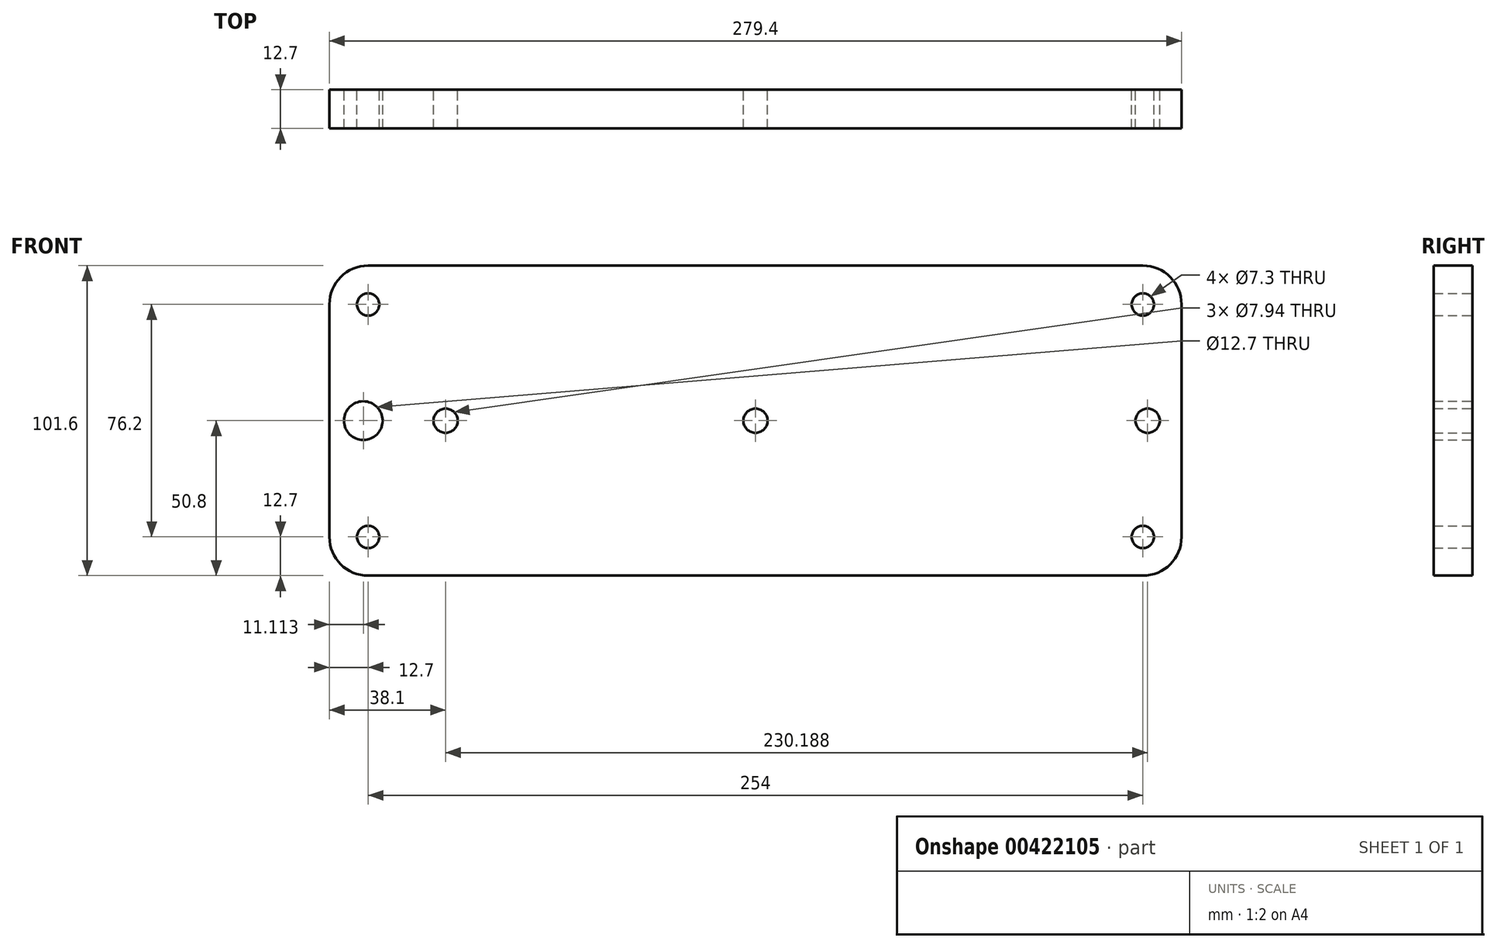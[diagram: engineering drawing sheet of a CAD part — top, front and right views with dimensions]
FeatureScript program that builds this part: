
annotation { "Feature Type Name" : "Feature", "Feature Type Description" : "" }
export const myFeature = defineFeature(function(context is Context, id is Id, definition is map)
    precondition{}
    {
        {
            var Q0;
            Q0=qCreatedBy(makeId("Front.planeOp"),FACE);
            var sketch = newSketch(context, id + "F0", { "sketchPlane" : qUnion([Q0])});
            skLineSegment(sketch, "E0.bottom", {"start": v(12.7, 0) * mm, "end": v(266.7, 0) * mm});
            skLineSegment(sketch, "E0.top", {"start": v(12.7, 101.6) * mm, "end": v(266.7, 101.6) * mm});
            skLineSegment(sketch, "E0.left", {"start": v(0, 12.7) * mm, "end": v(0, 88.9) * mm});
            skLineSegment(sketch, "E0.right", {"start": v(279.4, 12.7) * mm, "end": v(279.4, 88.9) * mm});
            skPoint(sketch, "E1.visualSharp", {"position": v(0, 101.6) * mm});
            skArc(sketch, "E1.filletArc", {"start": v(12.7, 101.6) * mm, "mid": v(3.72, 97.88) * mm, "end": v(0, 88.9) * mm});
            skPoint(sketch, "E2.visualSharp", {"position": v(0, 0) * mm});
            skArc(sketch, "E2.filletArc", {"start": v(0, 12.7) * mm, "mid": v(3.72, 3.72) * mm, "end": v(12.7, 0) * mm});
            skPoint(sketch, "E3.visualSharp", {"position": v(279.4, 101.6) * mm});
            skArc(sketch, "E3.filletArc", {"start": v(279.4, 88.9) * mm, "mid": v(275.68, 97.88) * mm, "end": v(266.7, 101.6) * mm});
            skPoint(sketch, "E4.visualSharp", {"position": v(279.4, 0) * mm});
            skArc(sketch, "E4.filletArc", {"start": v(266.7, 0) * mm, "mid": v(275.68, 3.72) * mm, "end": v(279.4, 12.7) * mm});
            skCircle(sketch, "E5", {"center": v(12.7, 88.9) * mm, "radius": 3.65 * mm});
            skCircle(sketch, "E6", {"center": v(12.7, 12.7) * mm, "radius": 3.65 * mm});
            skCircle(sketch, "E7", {"center": v(266.7, 88.9) * mm, "radius": 3.65 * mm});
            skCircle(sketch, "E8", {"center": v(266.7, 12.7) * mm, "radius": 3.65 * mm});
            skSolve(sketch);
        }
        {
            var Q0;
            Q0=makeQuery(id+"F0.imprint","IMPRINT",FACE,{"disambiguationData":[TD([[makeQuery(id+"F0.imprint","IMPRINT",EDGE,{"derivedFrom":sQuery(id+"F0.wireOp",EDGE,"E0.bottom")}),1.0]])]});
            var sketch = newSketch(context, id + "F1", { "sketchPlane" : qUnion([Q0])});
            skLineSegment(sketch, "E9", {"start": v(0, 0) * mm, "end": v(0, 50.8) * mm, "construction": true});
            skLineSegment(sketch, "E10", {"start": v(0, 50.8) * mm, "end": v(279.4, 50.8) * mm, "construction": true});
            skLineSegment(sketch, "E11", {"start": v(279.4, 50.8) * mm, "end": v(139.7, 50.8) * mm, "construction": true});
            skLineSegment(sketch, "E12", {"start": v(0, 50.8) * mm, "end": v(11.11, 50.8) * mm, "construction": true});
            skLineSegment(sketch, "E13", {"start": v(279.4, 50.8) * mm, "end": v(268.29, 50.8) * mm, "construction": true});
            skLineSegment(sketch, "E14", {"start": v(0, 50.8) * mm, "end": v(38.1, 50.8) * mm, "construction": true});
            skCircle(sketch, "E15", {"center": v(11.11, 50.8) * mm, "radius": 6.35 * mm});
            skCircle(sketch, "E16", {"center": v(38.1, 50.8) * mm, "radius": 3.97 * mm});
            skCircle(sketch, "E17", {"center": v(139.7, 50.8) * mm, "radius": 3.97 * mm});
            skCircle(sketch, "E18", {"center": v(268.29, 50.8) * mm, "radius": 3.97 * mm});
            skSolve(sketch);
        }
        {
            var Q0;
            Q0=makeQuery(id+"F0.imprint","IMPRINT",FACE,{"disambiguationData":[TD([[makeQuery(id+"F0.imprint","IMPRINT",EDGE,{"derivedFrom":sQuery(id+"F0.wireOp",EDGE,"E0.bottom")}),1.0]])]});
            extrude(context, id + "F2", {"entities" : qUnion([Q0]), "depth" : 12.7 * mm});
        }
        {
            var Q0;
            Q0 = qSketchRegion(id + "F1", true);
            extrude(context, id + "F3", {"entities" : qUnion([Q0]), "operationType" : NewBodyOperationType.REMOVE, "depth" : 25.4 * mm});
        }
    });
